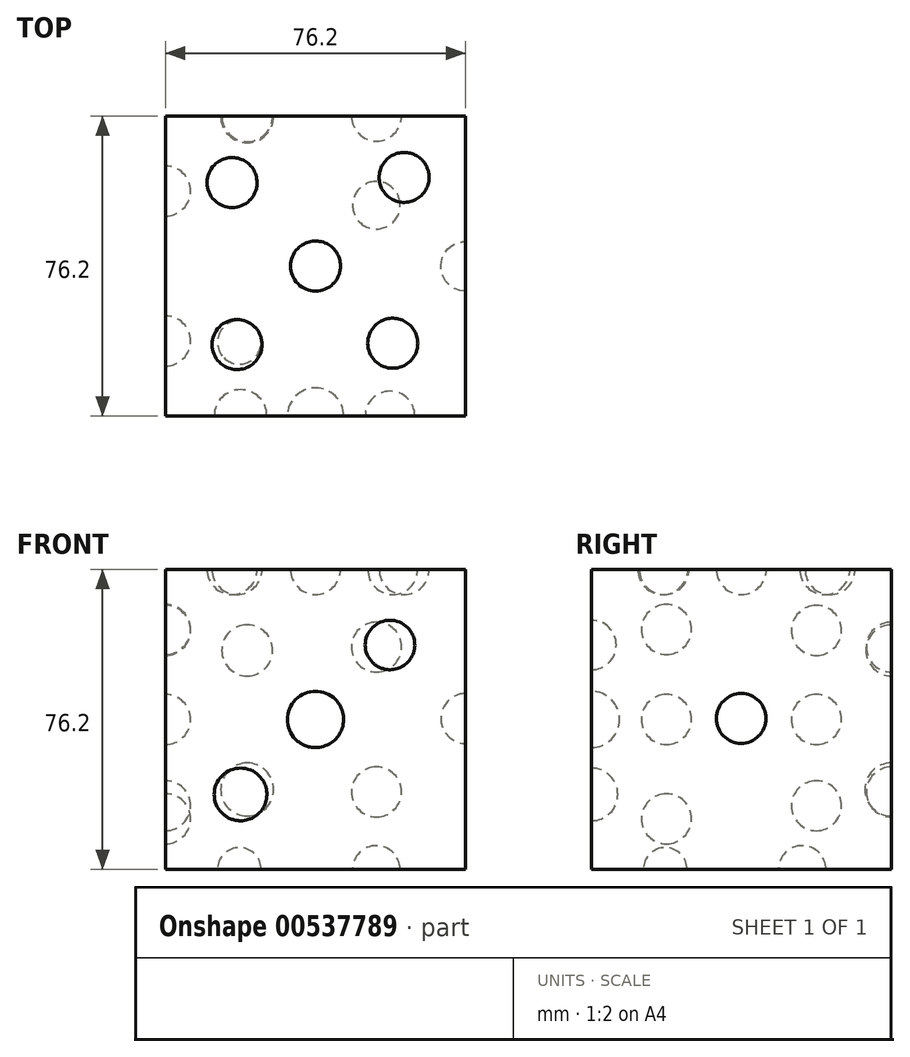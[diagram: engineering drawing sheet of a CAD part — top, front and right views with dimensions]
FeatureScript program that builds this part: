
annotation { "Feature Type Name" : "Feature", "Feature Type Description" : "" }
export const myFeature = defineFeature(function(context is Context, id is Id, definition is map)
    precondition{}
    {
        {
            var Q0;
            Q0=qCreatedBy(makeId("Front.planeOp"),FACE);
            var sketch = newSketch(context, id + "F0", { "sketchPlane" : qUnion([Q0])});
            skLineSegment(sketch, "E0.bottom", {"start": v(1.97, 0) * mm, "end": v(78.17, 0) * mm});
            skLineSegment(sketch, "E0.top", {"start": v(1.97, 76.2) * mm, "end": v(78.17, 76.2) * mm});
            skLineSegment(sketch, "E0.left", {"start": v(1.97, 0) * mm, "end": v(1.97, 76.2) * mm});
            skLineSegment(sketch, "E0.right", {"start": v(78.17, 0) * mm, "end": v(78.17, 76.2) * mm});
            skSolve(sketch);
        }
        {
            var Q0;
            Q0=qSketchRegion(id+"F0",true);
            extrude(context, id + "F1", {"entities" : qUnion([Q0]), "depth" : 76.2 * mm});
        }
        {
            var Q0;
            Q0=makeQuery(id+"F1.opExtrude","SWEPT_FACE",FACE,{"disambiguationData":[OSD([sQuery(id+"F0.wireOp",EDGE,"E0.right")])]});
            var sketch = newSketch(context, id + "F2", { "sketchPlane" : qUnion([Q0])});
            skArc(sketch, "E1", {"start": v(-38.18, 32) * mm, "mid": v(-31.88, 38.34) * mm, "end": v(-38.15, 44.7) * mm});
            skLineSegment(sketch, "E2", {"start": v(-38.1, 76.2) * mm, "end": v(-38.23, 0) * mm});
            skSolve(sketch);
        }
        {
            var Q0;
            {var subQ0=sQuery(id+"F2.wireOp",EDGE,"E1");Q0=makeQuery(id+"F2.imprint","IMPRINT",FACE,{"disambiguationData":[TD([[makeQuery(id+"F2.imprint","IMPRINT",EDGE,{"derivedFrom":subQ0}),1.0]])]});}
            var Q1;
            Q1=sQuery(id+"F2.wireOp",EDGE,"E2");
            revolve(context, id + "F3", {"operationType" : NewBodyOperationType.REMOVE, "entities" : qUnion([Q0]), "axis" : qUnion([Q1]), "revolveType" : RevolveType.FULL});
        }
        {
            var Q0;
            Q0=makeQuery(id+"F1.opExtrude","SWEPT_FACE",FACE,{"disambiguationData":[OSD([sQuery(id+"F0.wireOp",EDGE,"E0.left")])]});
            var sketch = newSketch(context, id + "F4", { "sketchPlane" : qUnion([Q0])});
            skLineSegment(sketch, "E3", {"start": v(0, 76.2) * mm, "end": v(38.1, 76.2) * mm});
            skLineSegment(sketch, "E4", {"start": v(19.05, 67.08) * mm, "end": v(19.05, 54.38) * mm});
            skLineSegment(sketch, "E5", {"start": v(38.1, 76.2) * mm, "end": v(76.2, 76.2) * mm});
            skLineSegment(sketch, "E6", {"start": v(57.15, 67.3) * mm, "end": v(57.15, 54.6) * mm});
            skArc(sketch, "E7", {"start": v(19.05, 54.38) * mm, "mid": v(25.4, 60.73) * mm, "end": v(19.05, 67.08) * mm});
            skArc(sketch, "E8", {"start": v(19.05, 31.75) * mm, "mid": v(25.4, 38.1) * mm, "end": v(19.05, 44.45) * mm});
            skArc(sketch, "E9", {"start": v(19.05, 9.83) * mm, "mid": v(25.4, 16.18) * mm, "end": v(19.05, 22.53) * mm});
            skArc(sketch, "E10", {"start": v(57.15, 54.6) * mm, "mid": v(63.5, 60.95) * mm, "end": v(57.15, 67.3) * mm});
            skArc(sketch, "E11", {"start": v(57.15, 31.75) * mm, "mid": v(63.5, 38.1) * mm, "end": v(57.15, 44.45) * mm});
            skArc(sketch, "E12", {"start": v(57.15, 6.5) * mm, "mid": v(63.5, 12.85) * mm, "end": v(57.15, 19.2) * mm});
            skPoint(sketch, "E13.orphan", {"position": v(19.05, 76.2) * mm});
            skLineSegment(sketch, "E14.trimOffspring", {"start": v(19.05, 44.45) * mm, "end": v(19.05, 31.75) * mm});
            skLineSegment(sketch, "E15.trimOffspring", {"start": v(19.05, 22.53) * mm, "end": v(19.05, 9.83) * mm});
            skPoint(sketch, "E16.orphan", {"position": v(19.05, 0) * mm});
            skPoint(sketch, "E17.orphan", {"position": v(57.15, 0) * mm});
            skLineSegment(sketch, "E18.trimOffspring", {"start": v(57.15, 19.2) * mm, "end": v(57.15, 6.5) * mm});
            skLineSegment(sketch, "E19.trimOffspring", {"start": v(57.15, 44.45) * mm, "end": v(57.15, 31.75) * mm});
            skPoint(sketch, "E20.orphan", {"position": v(57.15, 76.2) * mm});
            skSolve(sketch);
        }
        {
            var Q0;
            Q0=makeQuery(id+"F4.imprint","IMPRINT",FACE,{"disambiguationData":[TD([[makeQuery(id+"F4.imprint","IMPRINT",EDGE,{"derivedFrom":sQuery(id+"F4.wireOp",EDGE,"E4")}),1.0]])]});
            var Q1;
            Q1=makeQuery(id+"F4.imprint","IMPRINT",FACE,{"disambiguationData":[TD([[makeQuery(id+"F4.imprint","IMPRINT",EDGE,{"derivedFrom":sQuery(id+"F4.wireOp",EDGE,"E8")}),1.0]])]});
            var Q2;
            Q2=makeQuery(id+"F4.imprint","IMPRINT",FACE,{"disambiguationData":[TD([[makeQuery(id+"F4.imprint","IMPRINT",EDGE,{"derivedFrom":sQuery(id+"F4.wireOp",EDGE,"E9")}),1.0]])]});
            var Q3;
            Q3=sQuery(id+"F4.wireOp",EDGE,"E4");
            revolve(context, id + "F5", {"operationType" : NewBodyOperationType.REMOVE, "entities" : qUnion([Q0, Q1, Q2]), "axis" : qUnion([Q3]), "revolveType" : RevolveType.FULL, "oppositeDirection" : true});
        }
        {
            var Q0;
            Q0=makeQuery(id+"F4.imprint","IMPRINT",FACE,{"disambiguationData":[TD([[makeQuery(id+"F4.imprint","IMPRINT",EDGE,{"derivedFrom":sQuery(id+"F4.wireOp",EDGE,"E6")}),1.0]])]});
            var Q1;
            Q1=makeQuery(id+"F4.imprint","IMPRINT",FACE,{"disambiguationData":[TD([[makeQuery(id+"F4.imprint","IMPRINT",EDGE,{"derivedFrom":sQuery(id+"F4.wireOp",EDGE,"E11")}),1.0]])]});
            var Q2;
            Q2=makeQuery(id+"F4.imprint","IMPRINT",FACE,{"disambiguationData":[TD([[makeQuery(id+"F4.imprint","IMPRINT",EDGE,{"derivedFrom":sQuery(id+"F4.wireOp",EDGE,"E12")}),1.0]])]});
            var Q3;
            Q3=sQuery(id+"F4.wireOp",EDGE,"E6");
            revolve(context, id + "F6", {"operationType" : NewBodyOperationType.REMOVE, "entities" : qUnion([Q0, Q1, Q2]), "axis" : qUnion([Q3]), "revolveType" : RevolveType.FULL, "oppositeDirection" : true});
        }
        {
            var Q0;
            Q0=makeQuery(id+"F1.opExtrude","CAP_FACE",FACE,{"disambiguationData":[OSD([sQuery(id+"F0.wireOp",EDGE,"E0.bottom"),sQuery(id+"F0.wireOp",EDGE,"E0.top"),sQuery(id+"F0.wireOp",EDGE,"E0.left"),sQuery(id+"F0.wireOp",EDGE,"E0.right")])],"isStart":false});
            var sketch = newSketch(context, id + "F7", { "sketchPlane" : qUnion([Q0])});
            skLineSegment(sketch, "E21", {"start": v(63.44, 61.47) * mm, "end": v(54.54, 52.57) * mm});
            skLineSegment(sketch, "E22", {"start": v(16.29, 14.32) * mm, "end": v(25.75, 23.78) * mm});
            skLineSegment(sketch, "E23", {"start": v(40.07, 38.1) * mm, "end": v(35.02, 33.05) * mm});
            skLineSegment(sketch, "E24", {"start": v(40.07, 38.1) * mm, "end": v(45.12, 43.15) * mm});
            skArc(sketch, "E25", {"start": v(16.29, 14.32) * mm, "mid": v(25.75, 14.32) * mm, "end": v(25.75, 23.78) * mm});
            skArc(sketch, "E26", {"start": v(35.02, 33.05) * mm, "mid": v(45.12, 33.05) * mm, "end": v(45.12, 43.15) * mm});
            skArc(sketch, "E27", {"start": v(54.54, 52.57) * mm, "mid": v(63.44, 52.57) * mm, "end": v(63.44, 61.47) * mm});
            skLineSegment(sketch, "E28.trimOffspring", {"start": v(54.54, 52.57) * mm, "end": v(59, 57.02) * mm});
            skLineSegment(sketch, "E29.trimOffspring", {"start": v(25.75, 23.78) * mm, "end": v(21.02, 19.05) * mm});
            skPoint(sketch, "E30.orphan", {"position": v(1.97, 0) * mm});
            skLineSegment(sketch, "E31.trimOffspring", {"start": v(35.02, 33.05) * mm, "end": v(40.07, 38.1) * mm});
            skLineSegment(sketch, "E32.trimOffspring", {"start": v(45.12, 43.15) * mm, "end": v(35.02, 33.05) * mm});
            skLineSegment(sketch, "E33.trimOffspring", {"start": v(25.75, 23.78) * mm, "end": v(16.29, 14.32) * mm});
            skPoint(sketch, "E34.orphan", {"position": v(78.17, 76.2) * mm});
            skSolve(sketch);
        }
        {
            var Q0;
            {var subQ0=sQuery(id+"F7.wireOp",EDGE,"E25");Q0=makeQuery(id+"F7.imprint","IMPRINT",FACE,{"disambiguationData":[TD([[makeQuery(id+"F7.imprint","IMPRINT",EDGE,{"derivedFrom":subQ0}),1.0]])]});}
            var Q1;
            {var subQ0=sQuery(id+"F7.wireOp",EDGE,"E26");Q1=makeQuery(id+"F7.imprint","IMPRINT",FACE,{"disambiguationData":[TD([[makeQuery(id+"F7.imprint","IMPRINT",EDGE,{"derivedFrom":subQ0}),1.0]])]});}
            var Q2;
            Q2=makeQuery(id+"F7.imprint","IMPRINT",FACE,{"disambiguationData":[TD([[makeQuery(id+"F7.imprint","IMPRINT",EDGE,{"derivedFrom":sQuery(id+"F7.wireOp",EDGE,"E21")}),1.0]])]});
            var Q3;
            Q3=sQuery(id+"F7.wireOp",EDGE,"E33.trimOffspring");
            revolve(context, id + "F8", {"operationType" : NewBodyOperationType.REMOVE, "entities" : qUnion([Q0, Q1, Q2]), "axis" : qUnion([Q3]), "revolveType" : RevolveType.FULL, "oppositeDirection" : true});
        }
        {
            var Q0;
            Q0=makeQuery(id+"F1.opExtrude","CAP_FACE",FACE,{"disambiguationData":[OSD([sQuery(id+"F0.wireOp",EDGE,"E0.bottom"),sQuery(id+"F0.wireOp",EDGE,"E0.top"),sQuery(id+"F0.wireOp",EDGE,"E0.left"),sQuery(id+"F0.wireOp",EDGE,"E0.right")])],"isStart":true});
            var sketch = newSketch(context, id + "F9", { "sketchPlane" : qUnion([Q0])});
            skLineSegment(sketch, "E35", {"start": v(-58.06, 62.42) * mm, "end": v(-58.06, 48.88) * mm});
            skLineSegment(sketch, "E36", {"start": v(-58.06, 15.3) * mm, "end": v(-58.06, 30.29) * mm});
            skLineSegment(sketch, "E37", {"start": v(-22.71, 62.13) * mm, "end": v(-22.71, 49.18) * mm});
            skArc(sketch, "E38", {"start": v(-58.06, 48.88) * mm, "mid": v(-51.3, 55.65) * mm, "end": v(-58.06, 62.42) * mm});
            skArc(sketch, "E39", {"start": v(-58.06, 15.3) * mm, "mid": v(-50.57, 22.8) * mm, "end": v(-58.06, 30.29) * mm});
            skArc(sketch, "E40", {"start": v(-22.71, 49.18) * mm, "mid": v(-16.23, 55.65) * mm, "end": v(-22.71, 62.13) * mm});
            skArc(sketch, "E41", {"start": v(-22.71, 13.57) * mm, "mid": v(-15.98, 20.3) * mm, "end": v(-22.71, 27.04) * mm});
            skLineSegment(sketch, "E42.trimOffspring", {"start": v(-22.71, 27.04) * mm, "end": v(-22.71, 13.57) * mm});
            skPoint(sketch, "E43.orphan", {"position": v(-22.71, 0) * mm});
            skLineSegment(sketch, "E44.trimOffspring", {"start": v(-58.06, 48.88) * mm, "end": v(-58.06, 62.42) * mm});
            skPoint(sketch, "E45.orphan", {"position": v(-58.06, 0) * mm});
            skLineSegment(sketch, "E46.trimOffspring", {"start": v(-58.06, 30.29) * mm, "end": v(-58.06, 15.3) * mm});
            skSolve(sketch);
        }
        {
            var Q0;
            Q0=makeQuery(id+"F9.imprint","IMPRINT",FACE,{"disambiguationData":[TD([[makeQuery(id+"F9.imprint","IMPRINT",EDGE,{"derivedFrom":sQuery(id+"F9.wireOp",EDGE,"E37")}),1.0]])]});
            var Q1;
            Q1=makeQuery(id+"F9.imprint","IMPRINT",FACE,{"disambiguationData":[TD([[makeQuery(id+"F9.imprint","IMPRINT",EDGE,{"derivedFrom":sQuery(id+"F9.wireOp",EDGE,"E41")}),1.0]])]});
            var Q2;
            Q2=sQuery(id+"F9.wireOp",EDGE,"E37");
            revolve(context, id + "F10", {"operationType" : NewBodyOperationType.REMOVE, "entities" : qUnion([Q0, Q1]), "axis" : qUnion([Q2]), "revolveType" : RevolveType.FULL, "oppositeDirection" : true});
        }
        {
            var Q0;
            Q0=makeQuery(id+"F1.opExtrude","CAP_FACE",FACE,{"disambiguationData":[OSD([sQuery(id+"F0.wireOp",EDGE,"E0.bottom"),sQuery(id+"F0.wireOp",EDGE,"E0.top"),sQuery(id+"F0.wireOp",EDGE,"E0.left"),sQuery(id+"F0.wireOp",EDGE,"E0.right")])],"isStart":true});
            var sketch = newSketch(context, id + "F11", { "sketchPlane" : qUnion([Q0])});
            skLineSegment(sketch, "E47", {"start": v(-55.57, 62.83) * mm, "end": v(-55.57, 50.13) * mm});
            skArc(sketch, "E48", {"start": v(-55.57, 50.13) * mm, "mid": v(-49.22, 56.48) * mm, "end": v(-55.57, 62.83) * mm});
            skArc(sketch, "E49", {"start": v(-55.57, 13.33) * mm, "mid": v(-49.22, 19.68) * mm, "end": v(-55.57, 26.03) * mm});
            skLineSegment(sketch, "E50.trimOffspring", {"start": v(-55.57, 26.03) * mm, "end": v(-55.57, 13.33) * mm});
            skPoint(sketch, "E51.orphan", {"position": v(-55.57, 0) * mm});
            skSolve(sketch);
        }
        {
            var Q0;
            Q0=makeQuery(id+"F11.imprint","IMPRINT",FACE,{"disambiguationData":[TD([[makeQuery(id+"F11.imprint","IMPRINT",EDGE,{"derivedFrom":sQuery(id+"F11.wireOp",EDGE,"E47")}),1.0]])]});
            var Q1;
            Q1=makeQuery(id+"F11.imprint","IMPRINT",FACE,{"disambiguationData":[TD([[makeQuery(id+"F11.imprint","IMPRINT",EDGE,{"derivedFrom":sQuery(id+"F11.wireOp",EDGE,"E49")}),1.0]])]});
            var Q2;
            Q2=sQuery(id+"F11.wireOp",EDGE,"E47");
            revolve(context, id + "F12", {"operationType" : NewBodyOperationType.REMOVE, "entities" : qUnion([Q0, Q1]), "axis" : qUnion([Q2]), "revolveType" : RevolveType.FULL, "oppositeDirection" : true});
        }
        {
            var Q0;
            Q0=makeQuery(id+"F1.opExtrude","SWEPT_FACE",FACE,{"disambiguationData":[OSD([sQuery(id+"F0.wireOp",EDGE,"E0.bottom")])]});
            var sketch = newSketch(context, id + "F13", { "sketchPlane" : qUnion([Q0])});
            skLineSegment(sketch, "E52", {"start": v(16.78, 61.4) * mm, "end": v(24.62, 53.55) * mm});
            skArc(sketch, "E53", {"start": v(24.62, 53.55) * mm, "mid": v(24.62, 61.4) * mm, "end": v(16.78, 61.4) * mm});
            skArc(sketch, "E54", {"start": v(59.79, 18.38) * mm, "mid": v(59.79, 26.92) * mm, "end": v(51.25, 26.92) * mm});
            skLineSegment(sketch, "E55.trimOffspring", {"start": v(51.25, 26.92) * mm, "end": v(59.79, 18.38) * mm});
            skSolve(sketch);
        }
        {
            var Q0;
            Q0=makeQuery(id+"F13.imprint","IMPRINT",FACE,{"disambiguationData":[TD([[makeQuery(id+"F13.imprint","IMPRINT",EDGE,{"derivedFrom":sQuery(id+"F13.wireOp",EDGE,"E52")}),1.0]])]});
            var Q1;
            Q1=makeQuery(id+"F13.imprint","IMPRINT",FACE,{"disambiguationData":[TD([[makeQuery(id+"F13.imprint","IMPRINT",EDGE,{"derivedFrom":sQuery(id+"F13.wireOp",EDGE,"E54")}),1.0]])]});
            var Q2;
            Q2=sQuery(id+"F13.wireOp",EDGE,"E52");
            revolve(context, id + "F14", {"operationType" : NewBodyOperationType.REMOVE, "entities" : qUnion([Q0, Q1]), "axis" : qUnion([Q2]), "revolveType" : RevolveType.FULL, "oppositeDirection" : true});
        }
        {
            var Q0;
            Q0=makeQuery(id+"F1.opExtrude","SWEPT_FACE",FACE,{"disambiguationData":[OSD([sQuery(id+"F0.wireOp",EDGE,"E0.top")])]});
            var sketch = newSketch(context, id + "F15", { "sketchPlane" : qUnion([Q0])});
            skLineSegment(sketch, "E56", {"start": v(14.38, -12.41) * mm, "end": v(23.36, -21.4) * mm});
            skLineSegment(sketch, "E57", {"start": v(67.08, -11.1) * mm, "end": v(58.1, -20.07) * mm});
            skArc(sketch, "E58", {"start": v(23.36, -21.4) * mm, "mid": v(23.36, -12.41) * mm, "end": v(14.38, -12.41) * mm});
            skArc(sketch, "E59", {"start": v(67.08, -11.1) * mm, "mid": v(58.1, -11.1) * mm, "end": v(58.1, -20.07) * mm});
            skArc(sketch, "E60", {"start": v(44.56, -42.6) * mm, "mid": v(44.56, -33.6) * mm, "end": v(35.58, -33.6) * mm});
            skArc(sketch, "E61", {"start": v(64.18, -62.2) * mm, "mid": v(64.18, -53.23) * mm, "end": v(55.2, -53.23) * mm});
            skArc(sketch, "E62", {"start": v(24.6, -53.56) * mm, "mid": v(15.63, -53.56) * mm, "end": v(15.63, -62.54) * mm});
            skLineSegment(sketch, "E63.trimOffspring", {"start": v(24.6, -53.56) * mm, "end": v(15.63, -62.54) * mm});
            skPoint(sketch, "E64.orphan", {"position": v(1.97, -76.2) * mm});
            skPoint(sketch, "E65.orphan", {"position": v(78.17, 0) * mm});
            skLineSegment(sketch, "E66.trimOffspring", {"start": v(55.2, -53.23) * mm, "end": v(64.18, -62.2) * mm});
            skLineSegment(sketch, "E67.trimOffspring", {"start": v(35.58, -33.6) * mm, "end": v(44.56, -42.6) * mm});
            skSolve(sketch);
        }
        {
            var Q0;
            Q0=makeQuery(id+"F15.imprint","IMPRINT",FACE,{"disambiguationData":[TD([[makeQuery(id+"F15.imprint","IMPRINT",EDGE,{"derivedFrom":sQuery(id+"F15.wireOp",EDGE,"E56")}),1.0]])]});
            var Q1;
            Q1=makeQuery(id+"F15.imprint","IMPRINT",FACE,{"disambiguationData":[TD([[makeQuery(id+"F15.imprint","IMPRINT",EDGE,{"derivedFrom":sQuery(id+"F15.wireOp",EDGE,"E60")}),1.0]])]});
            var Q2;
            Q2=makeQuery(id+"F15.imprint","IMPRINT",FACE,{"disambiguationData":[TD([[makeQuery(id+"F15.imprint","IMPRINT",EDGE,{"derivedFrom":sQuery(id+"F15.wireOp",EDGE,"E61")}),1.0]])]});
            var Q3;
            Q3=sQuery(id+"F15.wireOp",EDGE,"E56");
            revolve(context, id + "F16", {"operationType" : NewBodyOperationType.REMOVE, "entities" : qUnion([Q0, Q1, Q2]), "axis" : qUnion([Q3]), "revolveType" : RevolveType.FULL, "oppositeDirection" : true});
        }
        {
            var Q0;
            Q0=makeQuery(id+"F15.imprint","IMPRINT",FACE,{"disambiguationData":[TD([[makeQuery(id+"F15.imprint","IMPRINT",EDGE,{"derivedFrom":sQuery(id+"F15.wireOp",EDGE,"E57")}),-1.0]])]});
            var Q1;
            Q1=makeQuery(id+"F15.imprint","IMPRINT",FACE,{"disambiguationData":[TD([[makeQuery(id+"F15.imprint","IMPRINT",EDGE,{"derivedFrom":sQuery(id+"F15.wireOp",EDGE,"E62")}),1.0]])]});
            var Q2;
            Q2=sQuery(id+"F15.wireOp",EDGE,"E57");
            revolve(context, id + "F17", {"operationType" : NewBodyOperationType.REMOVE, "entities" : qUnion([Q0, Q1]), "axis" : qUnion([Q2]), "revolveType" : RevolveType.FULL, "oppositeDirection" : true});
        }
    });
